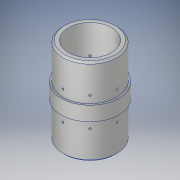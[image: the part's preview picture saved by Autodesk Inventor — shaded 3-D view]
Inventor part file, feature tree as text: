
AUTODESK INVENTOR PART (.ipt)
format: ipt  version: 2017 SP1 (Build 210196100, 196)  size: 208,896 bytes
history: native  units: in
note: dims shown in document units (in); Inventor stores cm internally (conversion verified against a paired STEP export)
features: sketch x4, extrude x3, plane x1, hole x1, pattern_circular x1, chamfer x1
ambient origin geometry x8: Origin, YZ Plane, XZ Plane, XY Plane, X Axis, Y Axis, Z Axis, Center Point
bodies: Solid1 (feature_tree)
feature tree (11):
  extrude  "Extrusion1"  Depth=4.0in
  extrude  "Extrusion2"  Depth=7.5in
  extrude  "Extrusion3"  Depth=6.0in TaperAngle=0.0deg
  plane  "Work Plane1"
  hole  "Hole1"  [1 undecoded]
  pattern_circular  "Circular Pattern1"  [2 undecoded]
  chamfer  "Chamfer1"  Distance=1.0in
  sketch  "Sketch1"  dims[d0=8.0in d1=4.0in]
  sketch  "Sketch2"  dims[d2=2.0in d3=0.0in d4=7.5in]
  sketch  "Sketch3"  dims[d5=6.0in d6=5.0in d7=0.0in]
  sketch  "Sketch4"  dims[d8=6.0in d9=7.5in d10=5.0in d11=0.0in d12=1.0in d13=1.0in d14=0.25in d15=0.75in d16=0.375in d17=0.25in d18=0.5635in d19=1.0in d20=0.8108in d21=3.1496in d22=360.0deg d24=0.25in d25=0.125in d26=45.0deg]
note: 3 required parameter values undecoded (feature->parameter linkage not recoverable at this tier; creation-order binding heuristic only, values carry confidence <= 0.55)
